# Revit family: E_Cable Junction Box_F_MEPcontent_Spelsberg_U 71 FD_INT-EN
name_source: partatom
category: Electrical Fixtures
revit_build: Autodesk Revit 2017 (Build: 20160225_1515(x64)
units: mm (PartAtom-declared; Revit-internal decimal feet)

## family parameters
Cut with Voids When Loaded = No
Host = Face
Maintain Annotation Orientation = Yes
OmniClass Number = 23.80.30.14.24
OmniClass Title = Junction Boxes
Part Type = Junction Box
Room Calculation Point = No
Round Connector Dimension = Use Diameter
Shared = No

## types (1)
- U 71 FD
    3D Representation = 3DGeometry : U 71 FD
    Article Description = Flat box U 71 FD
    Article Type = U 71 FD
    Conduit Diameter = 20 mm  [stored 0.0656168 ft]
    Default Elevation = 0 mm  [stored 0 ft]
    Description = Flat box U 71 FD
    ETIM Article Class = EC002601
    Height = 37.5 mm  [stored 0.123031 ft]
    IFCExportAs = IfcJunctionBox
    IFCExportType = NOTDEFINED
    Length = 71 mm  [stored 0.23294 ft]
    Manufacturer = Spelsberg
    Manufacturer Art. No. = 97103501
    Manufacturer URL = http://www.spelsberg.com
    Model = U 71 FD
    Placeholder Height = 36.5 mm  [stored 0.119751 ft]
    Product Line = Spelsberg
    Revit Version = 2017
    Rotation U-Axis Correction = 0.00°
    Rotation U-Axis Default Correction = 0.00°
    Rotation V-Axis Correction = 0.00°
    Rotation V-Axis Default Correction = 0.00°
    Rotation W-Axis Correction = 0.00°
    Rotation W-Axis Default Correction = 0.00°
    Voltage = 230 V
    Width = 71 mm  [stored 0.23294 ft]

note: [stored X ft] marks values corroborated as IEEE doubles in the binary element streams (Revit-internal decimal feet)

## geometry (parser evidence)
native form markers: Sweep x22
no freeform markers — native parametric forms only
